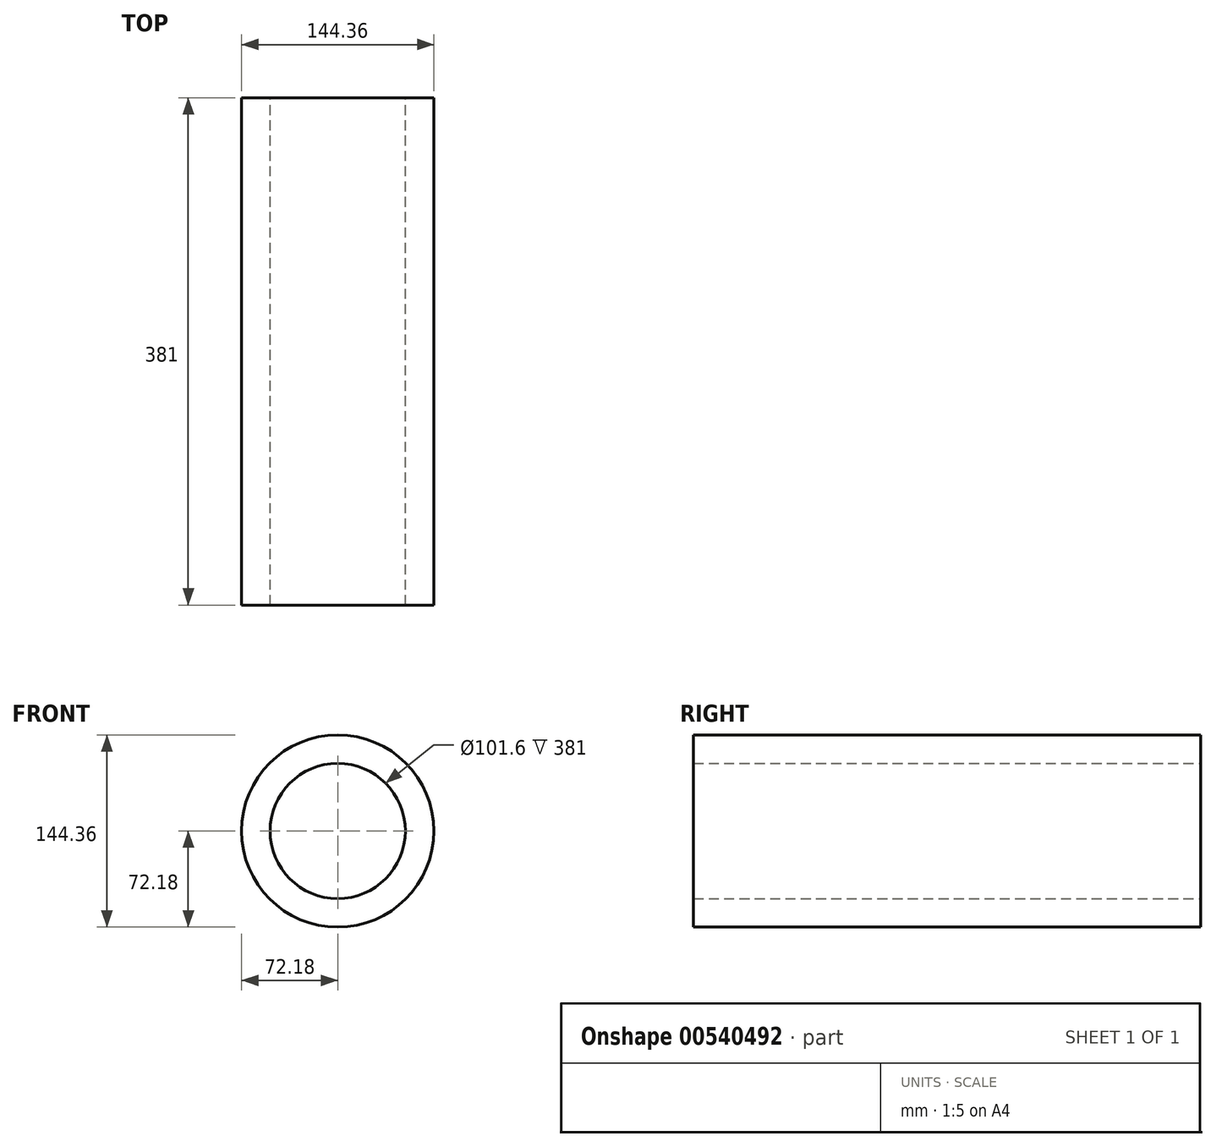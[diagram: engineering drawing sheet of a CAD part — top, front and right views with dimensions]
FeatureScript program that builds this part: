
annotation { "Feature Type Name" : "Feature", "Feature Type Description" : "" }
export const myFeature = defineFeature(function(context is Context, id is Id, definition is map)
    precondition{}
    {
        {
            var Q0;
            Q0=qCreatedBy(makeId("Front.planeOp"),FACE);
            var sketch = newSketch(context, id + "F0", { "sketchPlane" : qUnion([Q0])});
            skCircle(sketch, "E0", {"center": v(0, 0) * mm, "radius": 72.18 * mm});
            skSolve(sketch);
        }
        {
            var Q0;
            Q0=qCreatedBy(makeId("Front.planeOp"),FACE);
            var sketch = newSketch(context, id + "F1", { "sketchPlane" : qUnion([Q0])});
            skCircle(sketch, "E1", {"center": v(0, 0) * mm, "radius": 54.73 * mm});
            skSolve(sketch);
        }
        {
            var Q0;
            Q0=makeQuery(id+"F0.imprint","IMPRINT",FACE,{"disambiguationData":[TD([[makeQuery(id+"F0.imprint","IMPRINT",EDGE,{"derivedFrom":sQuery(id+"F0.wireOp",EDGE,"E0")}),1.0]])]});
            extrude(context, id + "F2", {"entities" : qUnion([Q0]), "depth" : 381 * mm, "offsetDistance" : 25.4 * mm});
        }
        {
            var Q0;
            Q0=sQuery(id+"F1.wireOp",VERTEX,"E1.center");
            var Q1;
            Q1=makeQuery(id+"F2.opExtrude","SWEPT_BODY",BODY,{"disambiguationData":[OSD([sQuery(id+"F0.wireOp",EDGE,"E0")])]});
            hole(context, id + "F3", {"style" : HoleStyle.SIMPLE, "endStyle" : HoleEndStyle.THROUGH, "oppositeDirection" : true, "holeDiameter" : 101.6 * mm, "isTappedThrough" : true, "tappedDepth" : 12.7 * mm, "tapClearance" : 3, "locations" : qUnion([Q0]), "scope" : qUnion([Q1])});
        }
    });
